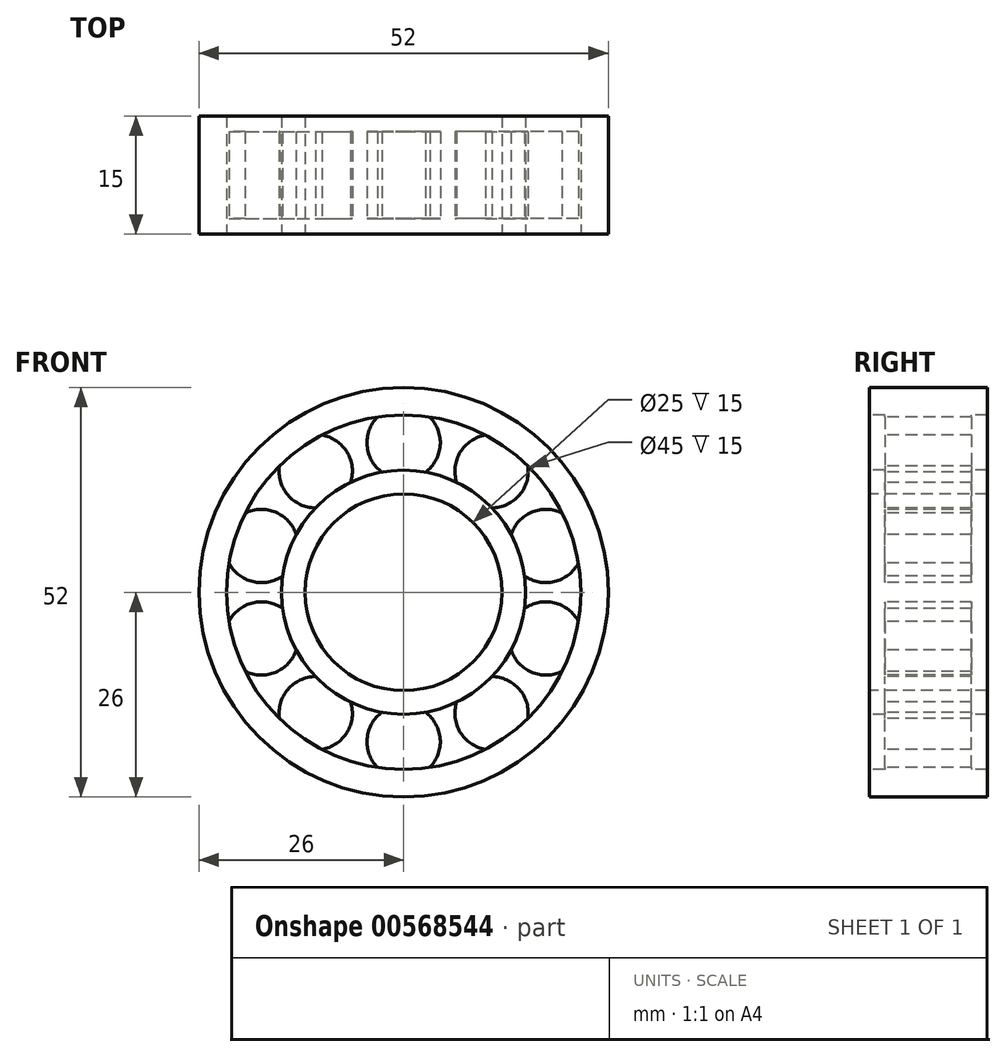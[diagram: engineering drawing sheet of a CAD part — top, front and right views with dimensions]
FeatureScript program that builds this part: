
annotation { "Feature Type Name" : "Feature", "Feature Type Description" : "" }
export const myFeature = defineFeature(function(context is Context, id is Id, definition is map)
    precondition{}
    {
        {
            var Q0;
            Q0=qCreatedBy(makeId("Front.planeOp"),FACE);
            var sketch = newSketch(context, id + "F0", { "sketchPlane" : qUnion([Q0])});
            skCircle(sketch, "E0", {"center": v(0, 0) * mm, "radius": 12.5 * mm});
            skCircle(sketch, "E1", {"center": v(0, 0) * mm, "radius": 15.5 * mm});
            skCircle(sketch, "E2", {"center": v(0, 0) * mm, "radius": 22.5 * mm});
            skCircle(sketch, "E3", {"center": v(0, 0) * mm, "radius": 26 * mm});
            skSolve(sketch);
        }
        {
            var Q0;
            Q0=makeQuery(id+"F0.imprint","IMPRINT",FACE,{"disambiguationData":[TD([[makeQuery(id+"F0.imprint","IMPRINT",EDGE,{"derivedFrom":sQuery(id+"F0.wireOp",EDGE,"E0")}),-1.0]])]});
            var Q1;
            Q1=makeQuery(id+"F0.imprint","IMPRINT",FACE,{"disambiguationData":[TD([[makeQuery(id+"F0.imprint","IMPRINT",EDGE,{"derivedFrom":sQuery(id+"F0.wireOp",EDGE,"E2")}),-1.0]])]});
            extrude(context, id + "F1", {"entities" : qUnion([Q0, Q1]), "oppositeDirection" : true, "depth" : 15 * mm, "offsetDistance" : 25 * mm});
        }
        {
            var Q0;
            Q0=qCreatedBy(makeId("Front.planeOp"),FACE);
            cPlane(context, id + "F2", {"entities" : qUnion([Q0]), "cplaneType" : CPlaneType.OFFSET, "offset" : 2 * mm, "oppositeDirection" : true, "width" : 150 * mm, "height" : 150 * mm});
        }
        {
            var Q0;
            Q0=qCreatedBy(id+"F2.planeOp",FACE);
            var sketch = newSketch(context, id + "F3", { "sketchPlane" : qUnion([Q0])});
            skCircle(sketch, "E4", {"center": v(0, 19) * mm, "radius": 4.66 * mm});
            skCircle(sketch, "E5.1.0", {"center": v(-11.17, 15.37) * mm, "radius": 4.66 * mm});
            skCircle(sketch, "E5.2.0", {"center": v(-18.07, 5.87) * mm, "radius": 4.66 * mm});
            skCircle(sketch, "E5.3.0", {"center": v(-18.07, -5.87) * mm, "radius": 4.66 * mm});
            skCircle(sketch, "E5.4.0", {"center": v(-11.17, -15.37) * mm, "radius": 4.66 * mm});
            skCircle(sketch, "E5.5.0", {"center": v(0, -19) * mm, "radius": 4.66 * mm});
            skCircle(sketch, "E5.6.0", {"center": v(11.17, -15.37) * mm, "radius": 4.66 * mm});
            skCircle(sketch, "E5.7.0", {"center": v(18.07, -5.87) * mm, "radius": 4.66 * mm});
            skCircle(sketch, "E5.8.0", {"center": v(18.07, 5.87) * mm, "radius": 4.66 * mm});
            skCircle(sketch, "E5.9.0", {"center": v(11.17, 15.37) * mm, "radius": 4.66 * mm});
            skPoint(sketch, "E5.center", {"position": v(0, 0) * mm});
            skSolve(sketch);
        }
        {
            var Q0;
            Q0 = qSketchRegion(id + "F3", true);
            extrude(context, id + "F4", {"entities" : qUnion([Q0]), "operationType" : NewBodyOperationType.ADD, "oppositeDirection" : true, "depth" : 11 * mm, "offsetDistance" : 25 * mm});
        }
    });
